# Revit family: BuzziShield Light - 2
name_source: partatom
category: Lighting Fixtures
units: mm (PartAtom-declared; Revit-internal decimal feet)

## family parameters
Always vertical = Yes
Cut with Voids When Loaded = No
Host = Ceiling
Light Source = Yes
OmniClass Number = 23.80.70.11
OmniClass Title = Luminaries for Internal Lighting
Part Type = Normal
Room Calculation Point = No
Round Connector Dimension = Use Diameter
Shared = No

## types (6) — shared parameters
Color Filter = 16777215
Dimming Lamp Color Temperature Shift = <None>
Light Source Symbol Size = 2' - 0"

## per-type parameters (varying)
| type | Emit from Line Length | Shade Height | Shade Type | Shade Width |
| M - 7.87" (20cm) Height | 2' - 9 3/8" | 0' - 7 7/8" | BuzziShield Light - Shade : M - 7.87" Height | 3' - 3 3/8" |
| M - 15.75" (40cm) Height | 2' - 9 3/8" | 1' - 3 3/4" | BuzziShield Light - Shade : M - 15.75" Height | 3' - 3 3/8" |
| M - 23.62" (60cm) Height | 2' - 9 3/8" | 1' - 11 5/8" | BuzziShield Light - Shade : M - 23.62" Height | 3' - 3 3/8" |
| L - 7.87" (20cm) Height | 4' - 1 1/8" | 0' - 7 7/8" | BuzziShield Light - Shade : L - 7.87" Height | 4' - 7 1/8" |
| L - 15.75" (40cm) Height | 4' - 1 1/8" | 1' - 3 3/4" | BuzziShield Light - Shade : L - 15.75" Height | 4' - 7 1/8" |
| L - 23.62" (60cm) Height | 4' - 1 1/8" | 1' - 11 5/8" | BuzziShield Light - Shade : L - 23.62" Height | 4' - 7 1/8" |

## geometry (parser evidence)
native form markers: Sweep x4
no freeform markers — native parametric forms only
